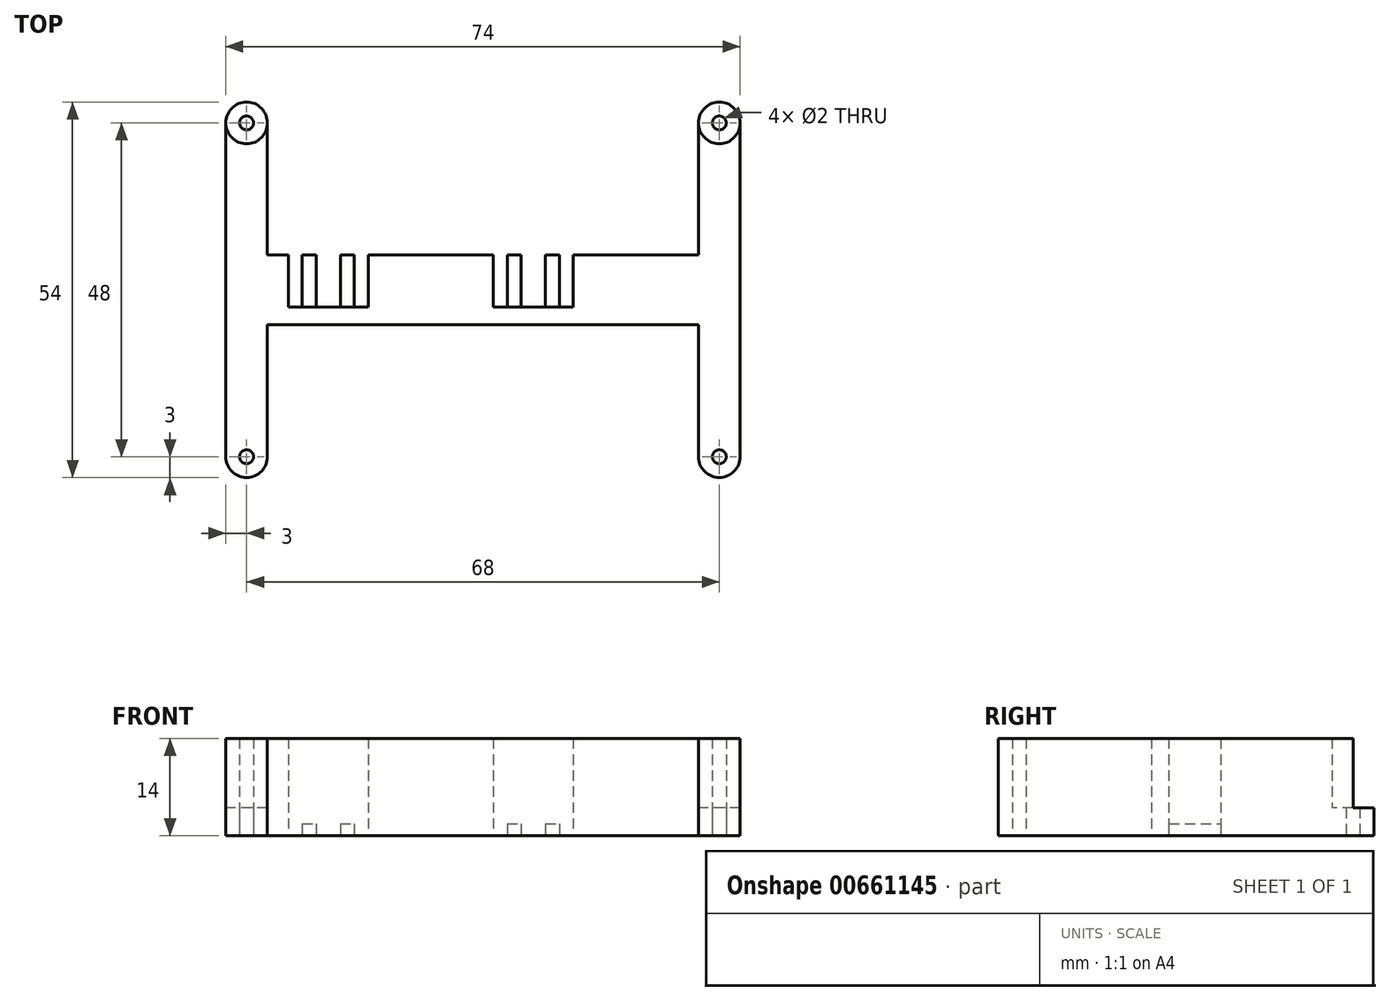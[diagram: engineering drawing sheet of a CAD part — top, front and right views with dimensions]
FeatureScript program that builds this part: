
annotation { "Feature Type Name" : "Feature", "Feature Type Description" : "" }
export const myFeature = defineFeature(function(context is Context, id is Id, definition is map)
    precondition{}
    {
        {
            var Q0;
            Q0=qCreatedBy(makeId("Top.planeOp"),FACE);
            var sketch = newSketch(context, id + "F0", { "sketchPlane" : qUnion([Q0])});
            skLineSegment(sketch, "E0", {"start": v(68, 0) * mm, "end": v(68, -19) * mm});
            skLineSegment(sketch, "E1", {"start": v(74, -19) * mm, "end": v(74, 29) * mm});
            skLineSegment(sketch, "E2", {"start": v(68, 29) * mm, "end": v(68, 10) * mm});
            skLineSegment(sketch, "E3", {"start": v(68, 10) * mm, "end": v(50, 10) * mm});
            skLineSegment(sketch, "E4", {"start": v(50, 10) * mm, "end": v(50, 2.5) * mm});
            skLineSegment(sketch, "E5", {"start": v(50, 2.5) * mm, "end": v(38.5, 2.5) * mm});
            skLineSegment(sketch, "E6", {"start": v(38.5, 2.5) * mm, "end": v(38.5, 10) * mm});
            skLineSegment(sketch, "E7", {"start": v(38.5, 10) * mm, "end": v(20.5, 10) * mm});
            skLineSegment(sketch, "E8", {"start": v(20.5, 10) * mm, "end": v(20.5, 2.5) * mm});
            skLineSegment(sketch, "E9", {"start": v(20.5, 2.5) * mm, "end": v(9, 2.5) * mm});
            skLineSegment(sketch, "E10", {"start": v(9, 2.5) * mm, "end": v(9, 10) * mm});
            skLineSegment(sketch, "E11", {"start": v(9, 10) * mm, "end": v(6, 10) * mm});
            skLineSegment(sketch, "E12", {"start": v(6, 10) * mm, "end": v(6, 29) * mm});
            skLineSegment(sketch, "E13", {"start": v(0, 29) * mm, "end": v(0, -19) * mm});
            skLineSegment(sketch, "E14", {"start": v(6, -19) * mm, "end": v(6, 0) * mm});
            skArc(sketch, "E15", {"start": v(0, 29) * mm, "mid": v(3, 32) * mm, "end": v(6, 29) * mm});
            skArc(sketch, "E16", {"start": v(6, -19) * mm, "mid": v(3, -22) * mm, "end": v(0, -19) * mm});
            skArc(sketch, "E17", {"start": v(74, -19) * mm, "mid": v(71, -22) * mm, "end": v(68, -19) * mm});
            skArc(sketch, "E18", {"start": v(68, 29) * mm, "mid": v(71, 32) * mm, "end": v(74, 29) * mm});
            skLineSegment(sketch, "E19", {"start": v(6, 0) * mm, "end": v(68, 0) * mm});
            skSolve(sketch);
        }
        {
            var Q0;
            Q0=makeQuery(id+"F0.imprint","IMPRINT",FACE,{"disambiguationData":[TD([[makeQuery(id+"F0.imprint","IMPRINT",EDGE,{"derivedFrom":sQuery(id+"F0.wireOp",EDGE,"E0")}),1.0]])]});
            extrude(context, id + "F1", {"entities" : qUnion([Q0]), "depth" : 4 * mm, "offsetDistance" : 25 * mm});
        }
        {
            var Q0;
            Q0=qCreatedBy(makeId("Top.planeOp"),FACE);
            var sketch = newSketch(context, id + "F2", { "sketchPlane" : qUnion([Q0])});
            skLineSegment(sketch, "E20.bottom", {"start": v(11, 2.5) * mm, "end": v(13, 2.5) * mm});
            skLineSegment(sketch, "E20.top", {"start": v(11, 10) * mm, "end": v(13, 10) * mm});
            skLineSegment(sketch, "E20.left", {"start": v(11, 2.5) * mm, "end": v(11, 10) * mm});
            skLineSegment(sketch, "E20.right", {"start": v(13, 2.5) * mm, "end": v(13, 10) * mm});
            skLineSegment(sketch, "E21.bottom", {"start": v(16.5, 2.5) * mm, "end": v(18.5, 2.5) * mm});
            skLineSegment(sketch, "E21.top", {"start": v(16.5, 10) * mm, "end": v(18.5, 10) * mm});
            skLineSegment(sketch, "E21.left", {"start": v(16.5, 2.5) * mm, "end": v(16.5, 10) * mm});
            skLineSegment(sketch, "E21.right", {"start": v(18.5, 2.5) * mm, "end": v(18.5, 10) * mm});
            skLineSegment(sketch, "E22.bottom", {"start": v(40.5, 2.5) * mm, "end": v(42.5, 2.5) * mm});
            skLineSegment(sketch, "E22.top", {"start": v(40.5, 10) * mm, "end": v(42.5, 10) * mm});
            skLineSegment(sketch, "E22.left", {"start": v(40.5, 2.5) * mm, "end": v(40.5, 10) * mm});
            skLineSegment(sketch, "E22.right", {"start": v(42.5, 2.5) * mm, "end": v(42.5, 10) * mm});
            skLineSegment(sketch, "E23.bottom", {"start": v(46, 2.5) * mm, "end": v(48, 2.5) * mm});
            skLineSegment(sketch, "E23.top", {"start": v(46, 10) * mm, "end": v(48, 10) * mm});
            skLineSegment(sketch, "E23.left", {"start": v(46, 2.5) * mm, "end": v(46, 10) * mm});
            skLineSegment(sketch, "E23.right", {"start": v(48, 2.5) * mm, "end": v(48, 10) * mm});
            skSolve(sketch);
        }
        {
            var Q0;
            Q0=makeQuery(id+"F2.imprint","IMPRINT",FACE,{"disambiguationData":[TD([[makeQuery(id+"F2.imprint","IMPRINT",EDGE,{"derivedFrom":sQuery(id+"F2.wireOp",EDGE,"E20.bottom")}),1.0]])]});
            var Q1;
            Q1=makeQuery(id+"F2.imprint","IMPRINT",FACE,{"disambiguationData":[TD([[makeQuery(id+"F2.imprint","IMPRINT",EDGE,{"derivedFrom":sQuery(id+"F2.wireOp",EDGE,"E21.bottom")}),1.0]])]});
            var Q2;
            Q2=makeQuery(id+"F2.imprint","IMPRINT",FACE,{"disambiguationData":[TD([[makeQuery(id+"F2.imprint","IMPRINT",EDGE,{"derivedFrom":sQuery(id+"F2.wireOp",EDGE,"E22.bottom")}),1.0]])]});
            var Q3;
            Q3=makeQuery(id+"F2.imprint","IMPRINT",FACE,{"disambiguationData":[TD([[makeQuery(id+"F2.imprint","IMPRINT",EDGE,{"derivedFrom":sQuery(id+"F2.wireOp",EDGE,"E23.bottom")}),1.0]])]});
            extrude(context, id + "F3", {"entities" : qUnion([Q0, Q1, Q2, Q3]), "operationType" : NewBodyOperationType.ADD, "depth" : 1.7 * mm, "offsetDistance" : 25 * mm});
        }
        {
            var Q0;
            Q0=makeQuery(id+"F1.opExtrude","CAP_FACE",FACE,{"disambiguationData":[OSD([sQuery(id+"F0.wireOp",EDGE,"E0"),sQuery(id+"F0.wireOp",EDGE,"E1"),sQuery(id+"F0.wireOp",EDGE,"E2"),sQuery(id+"F0.wireOp",EDGE,"E3"),sQuery(id+"F0.wireOp",EDGE,"E4"),sQuery(id+"F0.wireOp",EDGE,"E5"),sQuery(id+"F0.wireOp",EDGE,"E6"),sQuery(id+"F0.wireOp",EDGE,"E7"),sQuery(id+"F0.wireOp",EDGE,"E8"),sQuery(id+"F0.wireOp",EDGE,"E9"),sQuery(id+"F0.wireOp",EDGE,"E10"),sQuery(id+"F0.wireOp",EDGE,"E11"),sQuery(id+"F0.wireOp",EDGE,"E12"),sQuery(id+"F0.wireOp",EDGE,"E13"),sQuery(id+"F0.wireOp",EDGE,"E14"),sQuery(id+"F0.wireOp",EDGE,"E15"),sQuery(id+"F0.wireOp",EDGE,"E16"),sQuery(id+"F0.wireOp",EDGE,"E17"),sQuery(id+"F0.wireOp",EDGE,"E18"),sQuery(id+"F0.wireOp",EDGE,"E19")])],"isStart":false});
            var sketch = newSketch(context, id + "F4", { "sketchPlane" : qUnion([Q0])});
            skCircle(sketch, "E24", {"center": v(3, 29) * mm, "radius": 3 * mm});
            skCircle(sketch, "E25", {"center": v(71, 29) * mm, "radius": 3 * mm});
            skCircle(sketch, "E26", {"center": v(71, -19) * mm, "radius": 3 * mm});
            skCircle(sketch, "E27", {"center": v(3, -19) * mm, "radius": 3 * mm});
            skSolve(sketch);
        }
        {
            var Q0;
            {var subQ0=sQuery(id+"F4.wireOp",EDGE,"E24");Q0=makeQuery(id+"F4.imprint","IMPRINT",FACE,{"disambiguationData":[TD([[makeQuery(id+"F4.imprint","IMPRINT",EDGE,{"disambiguationData":[OD(0.0)],"derivedFrom":subQ0}),-1.0]])]});}
            var Q1;
            {var subQ0=sQuery(id+"F4.wireOp",EDGE,"E27");Q1=makeQuery(id+"F4.imprint","IMPRINT",FACE,{"disambiguationData":[TD([[makeQuery(id+"F4.imprint","IMPRINT",EDGE,{"disambiguationData":[OD(0.0)],"derivedFrom":subQ0}),1.0]])]});}
            var Q2;
            {var subQ0=sQuery(id+"F4.wireOp",EDGE,"E25");Q2=makeQuery(id+"F4.imprint","IMPRINT",FACE,{"disambiguationData":[TD([[makeQuery(id+"F4.imprint","IMPRINT",EDGE,{"disambiguationData":[OD(0.0)],"derivedFrom":subQ0}),-1.0]])]});}
            var Q3;
            {var subQ0=sQuery(id+"F4.wireOp",EDGE,"E26");Q3=makeQuery(id+"F4.imprint","IMPRINT",FACE,{"disambiguationData":[TD([[makeQuery(id+"F4.imprint","IMPRINT",EDGE,{"disambiguationData":[OD(0.0)],"derivedFrom":subQ0}),1.0]])]});}
            extrude(context, id + "F5", {"entities" : qUnion([Q0, Q1, Q2, Q3]), "operationType" : NewBodyOperationType.ADD, "depth" : 10 * mm, "offsetDistance" : 25 * mm});
        }
        {
            var Q0;
            Q0=makeQuery(id+"F3.boolean.opBoolean","MERGE",FACE,{"derivedFrom":[makeQuery(id+"F1.opExtrude","CAP_FACE",FACE,{"disambiguationData":[OSD([sQuery(id+"F0.wireOp",EDGE,"E0"),sQuery(id+"F0.wireOp",EDGE,"E1"),sQuery(id+"F0.wireOp",EDGE,"E2"),sQuery(id+"F0.wireOp",EDGE,"E3"),sQuery(id+"F0.wireOp",EDGE,"E4"),sQuery(id+"F0.wireOp",EDGE,"E5"),sQuery(id+"F0.wireOp",EDGE,"E6"),sQuery(id+"F0.wireOp",EDGE,"E7"),sQuery(id+"F0.wireOp",EDGE,"E8"),sQuery(id+"F0.wireOp",EDGE,"E9"),sQuery(id+"F0.wireOp",EDGE,"E10"),sQuery(id+"F0.wireOp",EDGE,"E11"),sQuery(id+"F0.wireOp",EDGE,"E12"),sQuery(id+"F0.wireOp",EDGE,"E13"),sQuery(id+"F0.wireOp",EDGE,"E14"),sQuery(id+"F0.wireOp",EDGE,"E15"),sQuery(id+"F0.wireOp",EDGE,"E16"),sQuery(id+"F0.wireOp",EDGE,"E17"),sQuery(id+"F0.wireOp",EDGE,"E18"),sQuery(id+"F0.wireOp",EDGE,"E19")])],"isStart":true}),makeQuery(id+"F3.opExtrude","CAP_FACE",FACE,{"disambiguationData":[OSD([sQuery(id+"F2.wireOp",EDGE,"E20.bottom"),sQuery(id+"F2.wireOp",EDGE,"E20.top"),sQuery(id+"F2.wireOp",EDGE,"E20.left"),sQuery(id+"F2.wireOp",EDGE,"E20.right")])],"isStart":true}),makeQuery(id+"F3.opExtrude","CAP_FACE",FACE,{"disambiguationData":[OSD([sQuery(id+"F2.wireOp",EDGE,"E21.bottom"),sQuery(id+"F2.wireOp",EDGE,"E21.top"),sQuery(id+"F2.wireOp",EDGE,"E21.left"),sQuery(id+"F2.wireOp",EDGE,"E21.right")])],"isStart":true}),makeQuery(id+"F3.opExtrude","CAP_FACE",FACE,{"disambiguationData":[OSD([sQuery(id+"F2.wireOp",EDGE,"E22.bottom"),sQuery(id+"F2.wireOp",EDGE,"E22.top"),sQuery(id+"F2.wireOp",EDGE,"E22.left"),sQuery(id+"F2.wireOp",EDGE,"E22.right")])],"isStart":true}),makeQuery(id+"F3.opExtrude","CAP_FACE",FACE,{"disambiguationData":[OSD([sQuery(id+"F2.wireOp",EDGE,"E23.bottom"),sQuery(id+"F2.wireOp",EDGE,"E23.top"),sQuery(id+"F2.wireOp",EDGE,"E23.left"),sQuery(id+"F2.wireOp",EDGE,"E23.right")])],"isStart":true})]});
            var sketch = newSketch(context, id + "F6", { "sketchPlane" : qUnion([Q0])});
            skCircle(sketch, "E28", {"center": v(3, 19) * mm, "radius": 1 * mm});
            skCircle(sketch, "E29", {"center": v(71, 19) * mm, "radius": 1 * mm});
            skCircle(sketch, "E30", {"center": v(71, -29) * mm, "radius": 1 * mm});
            skCircle(sketch, "E31", {"center": v(3, -29) * mm, "radius": 1 * mm});
            skSolve(sketch);
        }
        {
            var Q0;
            Q0 = qSketchRegion(id + "F6", true);
            extrude(context, id + "F7", {"entities" : qUnion([Q0]), "operationType" : NewBodyOperationType.REMOVE, "oppositeDirection" : true, "depth" : 25 * mm, "offsetDistance" : 25 * mm});
        }
    });
